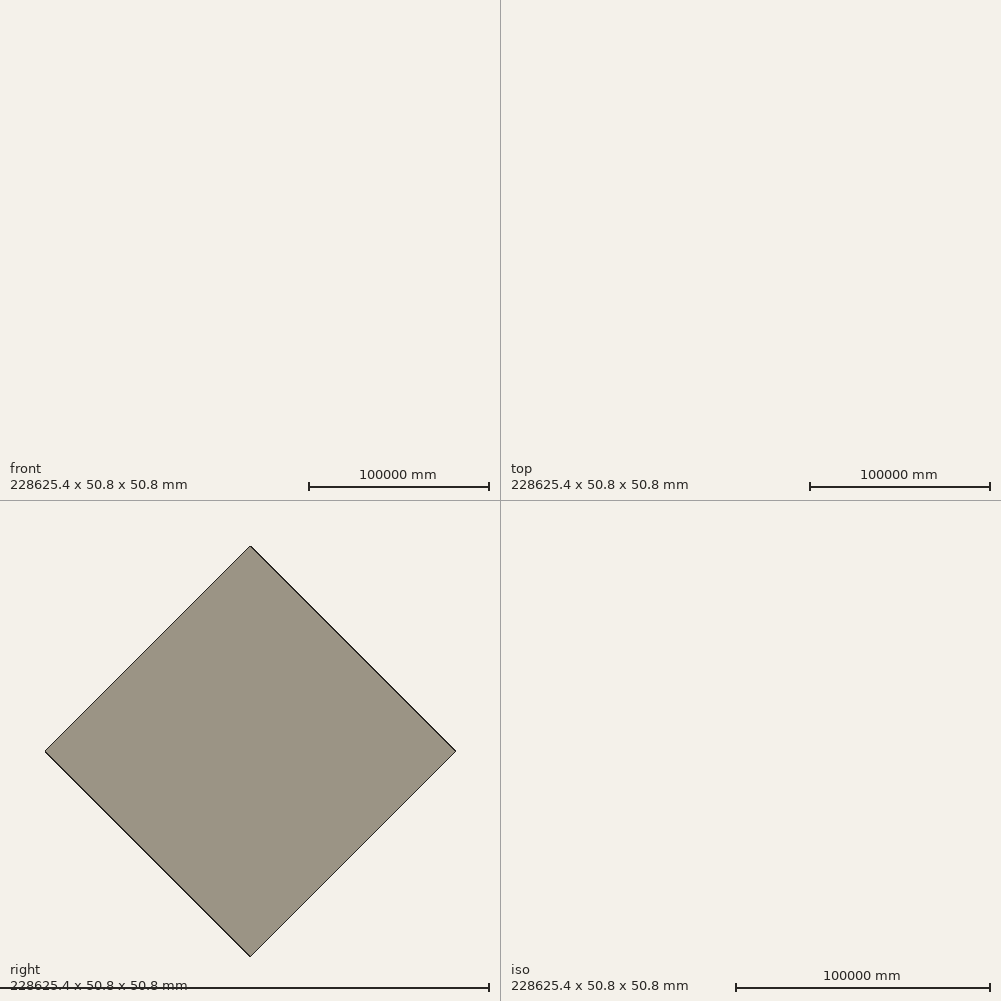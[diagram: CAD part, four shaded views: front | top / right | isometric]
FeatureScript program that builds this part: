
annotation { "Feature Type Name" : "Feature", "Feature Type Description" : "" }
export const myFeature = defineFeature(function(context is Context, id is Id, definition is map)
    precondition{}
    {
        {
            var Q0;
            Q0=qCreatedBy(makeId("Right.planeOp"),FACE);
            var sketch = newSketch(context, id + "F0", { "sketchPlane" : qUnion([Q0])});
            skCircle(sketch, "E0", {"center": v(0, 0) * mm, "radius": 25.4 * mm});
            skSolve(sketch);
        }
        {
            var Q0;
            Q0 = qSketchRegion(id + "F0", true);
            extrude(context, id + "F1", {"entities" : qUnion([Q0]), "depth" : 228625.4 * mm});
        }
    });
